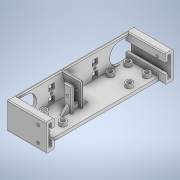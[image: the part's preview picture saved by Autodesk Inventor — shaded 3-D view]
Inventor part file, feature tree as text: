
AUTODESK INVENTOR PART (.ipt)
format: ipt  version: 2022 (Build 260153000, 153)  size: 440,832 bytes
history: native  units: in
note: dims shown in document units (in); Inventor stores cm internally (conversion verified against a paired STEP export)
features: extrude x14, sketch x14, mirror x1, fillet x1
ambient origin geometry x8: Origin, YZ Plane, XZ Plane, XY Plane, X Axis, Y Axis, Z Axis, Center Point
bodies: Solid1 (feature_tree)
feature tree (30):
  extrude  "Extrusion1"  Depth=7.4016in
  extrude  "Extrusion2"  Depth=0.1575in
  extrude  "Extrusion3"  Depth=0.1575in
  sketch  "Sketch4"  dims[d7=0.1575in d8=0.1575in]
  extrude  "Extrusion4"  Depth=0.1575in
  extrude  "Extrusion5"  Depth=0.315in
  extrude  "Extrusion6"  Depth=0.1575in
  extrude  "Extrusion7"  Depth=0.1575in
  sketch  "Sketch8"  dims[d16=0.315in d17=2.126in d18=0.0in]
  extrude  "Extrusion9"  Depth=2.126in TaperAngle=0.0deg
  extrude  "Extrusion10"  Depth=0.6102in
  extrude  "Extrusion11"  Depth=0.2362in
  extrude  "Extrusion12"  Depth=0.2362in
  extrude  "Extrusion13"  Depth=0.6299in
  extrude  "Extrusion14"  Depth=0.3937in
  extrude  "Extrusion15"  Depth=0.3937in
  mirror  "Mirror2"
  fillet  "Fillet1"  Radius=0.3937in
  sketch  "Sketch1"  dims[d0=1.8898in d1=7.4016in]
  sketch  "Sketch2"  dims[d2=0.1969in d3=0.0in d4=0.1575in]
  sketch  "Sketch3"  dims[d5=0.1575in d6=0.1575in]
  sketch  "Sketch5"  dims[d9=1.378in d10=0.0in d11=0.315in]
  sketch  "Sketch6"  dims[d12=0.1575in d13=0.1575in]
  sketch  "Sketch7"  dims[d14=0.315in d15=0.1575in]
  sketch  "Sketch9"  dims[d19=0.4921in d20=0.6102in]
  sketch  "Sketch10"  dims[d21=0.2362in d22=0.2362in]
  sketch  "Sketch11"  dims[d23=0.2362in d24=0.2362in]
  sketch  "Sketch12"  dims[d25=2.126in d26=0.0in d28=0.6299in]
  sketch  "Sketch13"  dims[d29=1.378in d30=0.0in d31=0.3937in]
  sketch  "Sketch14"  dims[d32=0.3937in d33=0.3937in d34=0.3937in d35=0.1969in d36=0.0in d37=0.1969in d38=0.0in d42=0.6299in d43=0.1575in d44=0.3937in d45=0.3937in d46=1.1024in d47=0.0in d48=0.0in d49=0.1575in d50=0.7087in d51=0.0in d52=0.1575in d53=0.0in d54=0.1969in d55=0.0in d56=0.1181in d57=0.1969in d58=0.0in d59=0.1575in d60=0.1575in d61=0.4724in d62=0.0in d63=0.4528in d64=0.4528in d65=0.315in d66=0.315in d67=0.315in d68=0.315in d69=0.1575in d70=0.1575in d71=0.0in d72=0.0591in d73=2.5197in d74=3.0709in]
